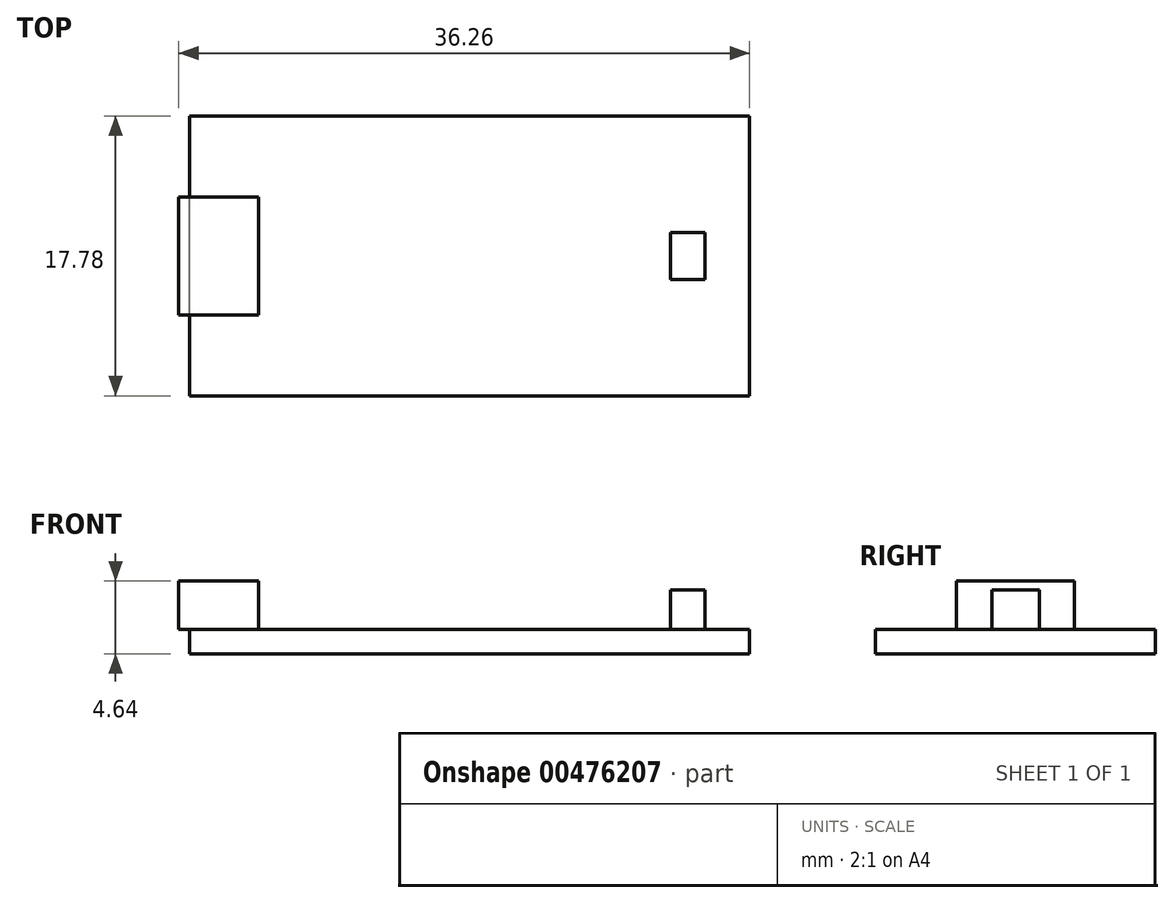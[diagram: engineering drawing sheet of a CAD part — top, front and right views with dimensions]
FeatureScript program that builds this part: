
annotation { "Feature Type Name" : "Feature", "Feature Type Description" : "" }
export const myFeature = defineFeature(function(context is Context, id is Id, definition is map)
    precondition{}
    {
        {
            var Q0;
            Q0=qCreatedBy(makeId("Top.planeOp"),FACE);
            var sketch = newSketch(context, id + "F0", { "sketchPlane" : qUnion([Q0])});
            skLineSegment(sketch, "E0.bottom", {"start": v(17.78, -8.9) * mm, "end": v(-17.78, -8.9) * mm});
            skLineSegment(sketch, "E0.top", {"start": v(17.78, 8.9) * mm, "end": v(-17.78, 8.9) * mm});
            skLineSegment(sketch, "E0.left", {"start": v(17.78, -8.9) * mm, "end": v(17.78, 8.89) * mm});
            skLineSegment(sketch, "E0.right", {"start": v(-17.78, -8.9) * mm, "end": v(-17.78, 8.89) * mm});
            skPoint(sketch, "E0.middle", {"position": v(0, 0) * mm});
            skSolve(sketch);
        }
        {
            var Q0;
            Q0=makeQuery(id+"F0.imprint","IMPRINT",FACE,{"disambiguationData":[TD([[makeQuery(id+"F0.imprint","IMPRINT",EDGE,{"derivedFrom":sQuery(id+"F0.wireOp",EDGE,"E0.bottom")}),-1.0]])]});
            extrude(context, id + "F1", {"entities" : qUnion([Q0]), "depth" : 1.57 * mm});
        }
        {
            var Q0;
            Q0=makeQuery(id+"F1.opExtrude","CAP_FACE",FACE,{"disambiguationData":[OSD([sQuery(id+"F0.wireOp",EDGE,"E0.bottom"),sQuery(id+"F0.wireOp",EDGE,"E0.top"),sQuery(id+"F0.wireOp",EDGE,"E0.left"),sQuery(id+"F0.wireOp",EDGE,"E0.right")])],"isStart":false});
            var sketch = newSketch(context, id + "F2", { "sketchPlane" : qUnion([Q0])});
            skLineSegment(sketch, "E1", {"start": v(-17.78, 0) * mm, "end": v(17.78, 0) * mm});
            skLineSegment(sketch, "E2.bottom", {"start": v(-13.42, -3.75) * mm, "end": v(-18.48, -3.75) * mm});
            skLineSegment(sketch, "E2.top", {"start": v(-13.42, 3.75) * mm, "end": v(-18.48, 3.75) * mm});
            skLineSegment(sketch, "E2.left", {"start": v(-13.42, -3.75) * mm, "end": v(-13.42, 3.75) * mm});
            skLineSegment(sketch, "E2.right", {"start": v(-18.48, -3.75) * mm, "end": v(-18.48, 3.75) * mm});
            skPoint(sketch, "E2.middle", {"position": v(-15.95, 0) * mm});
            skLineSegment(sketch, "E3.bottom", {"start": v(14.94, -1.5) * mm, "end": v(12.74, -1.5) * mm});
            skLineSegment(sketch, "E3.top", {"start": v(14.94, 1.5) * mm, "end": v(12.74, 1.5) * mm});
            skLineSegment(sketch, "E3.left", {"start": v(14.94, -1.5) * mm, "end": v(14.94, 1.5) * mm});
            skLineSegment(sketch, "E3.right", {"start": v(12.74, -1.5) * mm, "end": v(12.74, 1.5) * mm});
            skPoint(sketch, "E3.middle", {"position": v(13.84, 0) * mm});
            skSolve(sketch);
        }
        {
            var Q0;
            {var subQ0=sQuery(id+"F2.wireOp",EDGE,"E1");var subQ1=makeQuery(id+"F1.opExtrude","CAP_EDGE",EDGE,{"disambiguationData":[OSD([sQuery(id+"F0.wireOp",EDGE,"E0.right")])],"isStart":false});var subQ2=makeQuery(id+"F2.imprint","INTERSECT",VERTEX,{"derivedFrom":[subQ1,subQ0]});Q0=makeQuery(id+"F2.imprint","IMPRINT",FACE,{"disambiguationData":[TD([[makeQuery(id+"F2.imprint","IMPRINT",EDGE,{"disambiguationData":[TD([[subQ2,-1.0]])],"derivedFrom":subQ0}),1.0]])]});}
            var Q1;
            {var subQ4=sQuery(id+"F2.wireOp",EDGE,"E2.right");Q1=makeQuery(id+"F2.imprint","IMPRINT",FACE,{"disambiguationData":[TD([[makeQuery(id+"F2.imprint","IMPRINT",EDGE,{"derivedFrom":subQ4}),-1.0]])]});}
            var Q2;
            {var subQ0=sQuery(id+"F2.wireOp",EDGE,"E1");var subQ1=makeQuery(id+"F1.opExtrude","CAP_EDGE",EDGE,{"disambiguationData":[OSD([sQuery(id+"F0.wireOp",EDGE,"E0.right")])],"isStart":false});var subQ2=makeQuery(id+"F2.imprint","INTERSECT",VERTEX,{"derivedFrom":[subQ1,subQ0]});Q2=makeQuery(id+"F2.imprint","IMPRINT",FACE,{"disambiguationData":[TD([[makeQuery(id+"F2.imprint","IMPRINT",EDGE,{"disambiguationData":[TD([[subQ2,-1.0]])],"derivedFrom":subQ0}),-1.0]])]});}
            extrude(context, id + "F3", {"entities" : qUnion([Q0, Q1, Q2]), "operationType" : NewBodyOperationType.ADD, "depth" : 3.07 * mm});
        }
        {
            var Q0;
            {var subQ5=sQuery(id+"F2.wireOp",EDGE,"E3.top");Q0=makeQuery(id+"F2.imprint","IMPRINT",FACE,{"disambiguationData":[TD([[makeQuery(id+"F2.imprint","IMPRINT",EDGE,{"derivedFrom":subQ5}),1.0]])]});}
            var Q1;
            {var subQ5=sQuery(id+"F2.wireOp",EDGE,"E3.bottom");Q1=makeQuery(id+"F2.imprint","IMPRINT",FACE,{"disambiguationData":[TD([[makeQuery(id+"F2.imprint","IMPRINT",EDGE,{"derivedFrom":subQ5}),-1.0]])]});}
            extrude(context, id + "F4", {"entities" : qUnion([Q0, Q1]), "operationType" : NewBodyOperationType.ADD, "depth" : 2.5 * mm});
        }
    });
